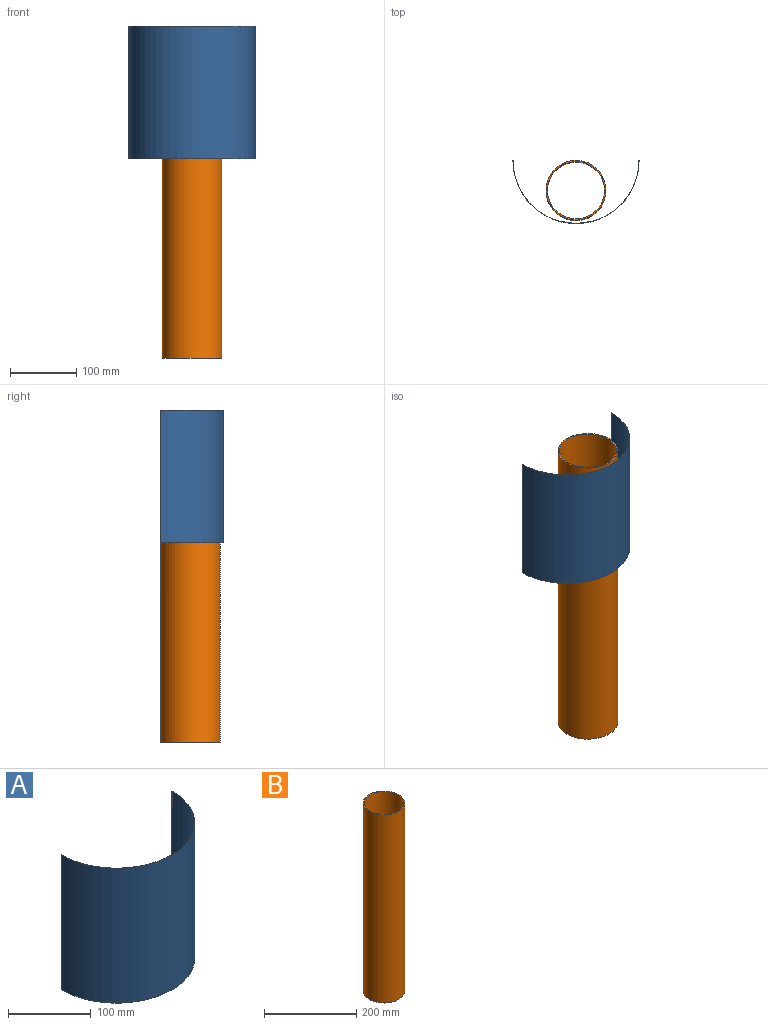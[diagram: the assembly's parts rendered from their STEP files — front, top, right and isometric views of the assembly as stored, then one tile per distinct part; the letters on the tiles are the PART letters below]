
ASSEMBLY  parts=2 mates=1
PART A: 6 faces, bbox 190x95x200 mm
  f0: plane 200x0.3mm, normal (0,1,0), area 60mm2, adj f1,f3,f4,f5
  f1: cylinder r=95mm len=200mm, axis (0,0,-1), area 59690.3mm2, adj f0,f2,f4,f5
  f2: plane 200x0.3mm, normal (0,1,0), area 60mm2, adj f1,f3,f4,f5
  f3: cylinder r=94.7mm len=200mm, axis (0,0,-1), area 59501.8mm2, adj f0,f2,f4,f5
  f4: plane 190x95mm, normal (0,0,1), area 89.4mm2, adj f0,f1,f2,f3
  f5: plane 190x95mm, normal (0,0,-1), area 89.4mm2, adj f0,f1,f2,f3
PART B: 4 faces, bbox 90x90x500 mm
  f0: cylinder r=43mm len=500mm, axis (0,0,-1), area 135088.5mm2, adj f2,f3
  f1: cylinder r=45mm len=500mm, axis (0,0,-1), area 141371.7mm2, adj f2,f3
  f2: plane 90x90mm, normal (0,0,-1), area 552.9mm2, adj f0,f1
  f3: plane 90x90mm, normal (0,0,1), area 552.9mm2, adj f0,f1
PLACE A t=(18.45,99.93,116.41)mm
PLACE B t=(18.45,54.93,-183.59)mm
MATE fastened A.f3 <-> B.f3  axis (0,0,1) through (18.45,99.93,316.41)mm
